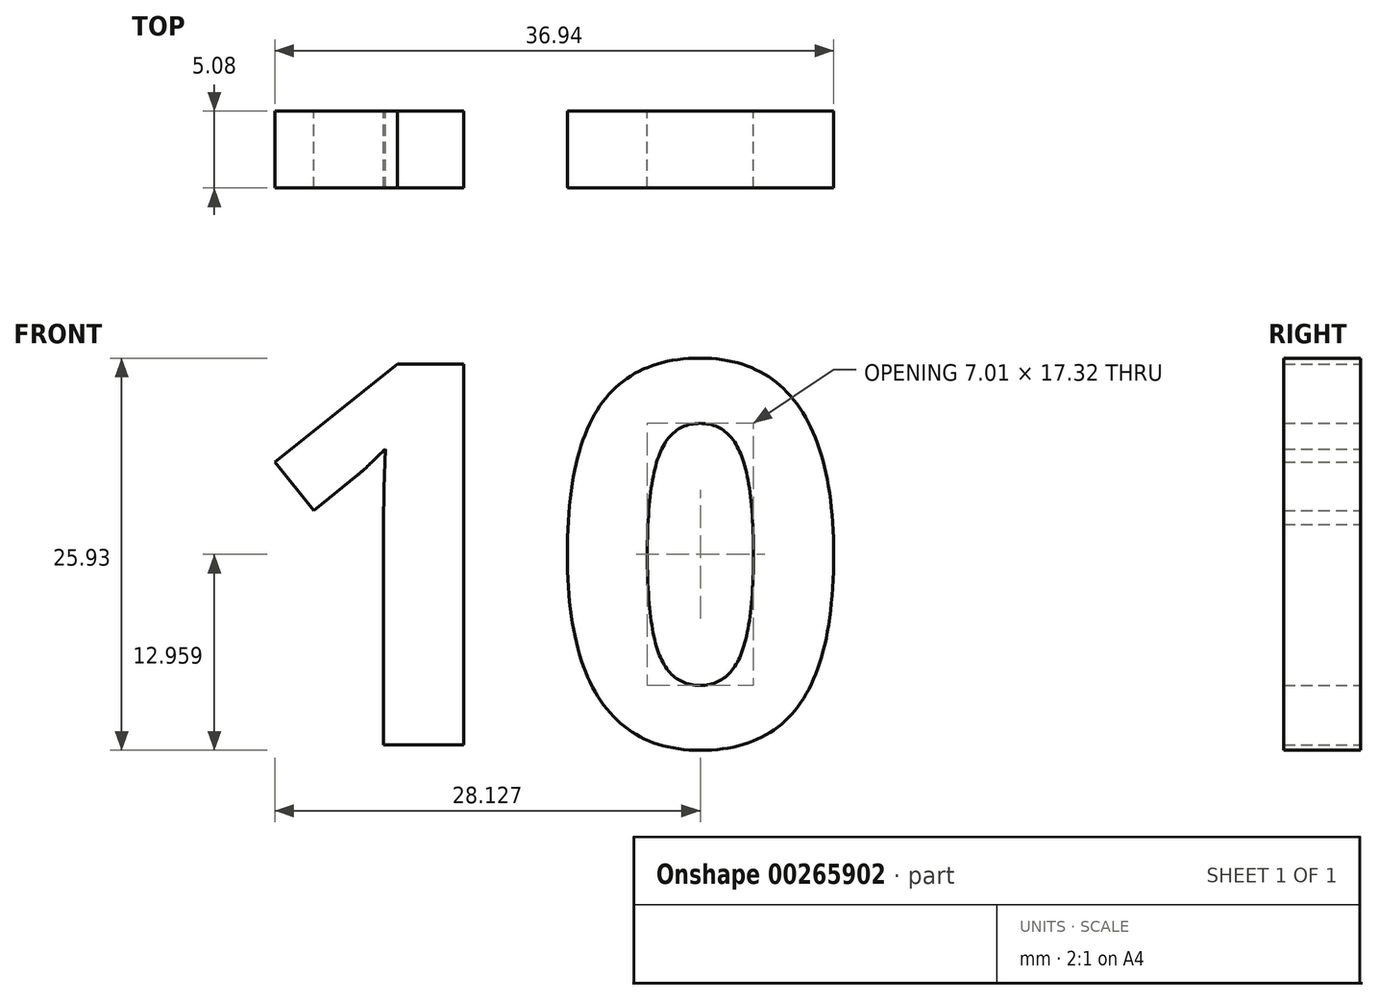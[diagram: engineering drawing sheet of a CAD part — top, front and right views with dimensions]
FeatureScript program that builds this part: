
annotation { "Feature Type Name" : "Feature", "Feature Type Description" : "" }
export const myFeature = defineFeature(function(context is Context, id is Id, definition is map)
    precondition{}
    {
        {
            var Q0;
            Q0=qCreatedBy(makeId("Front.planeOp"),FACE);
            var sketch = newSketch(context, id + "F0", { "sketchPlane" : qUnion([Q0])});
            skText(sketch, "E0", { "text": "10", "fontName": "OpenSans-Bold.ttf"});
            const initialGuessF0  = {"E0": [-0.0716, 0.0357, 1, 0, 0.0254]};
            skSetInitialGuess(sketch, initialGuessF0);
            skSolve(sketch);
        }
        {
            var Q0;
            Q0 = qSketchRegion(id + "F0", true);
            extrude(context, id + "F1", {"entities" : qUnion([Q0]), "depth" : 5.08 * mm});
        }
    });
